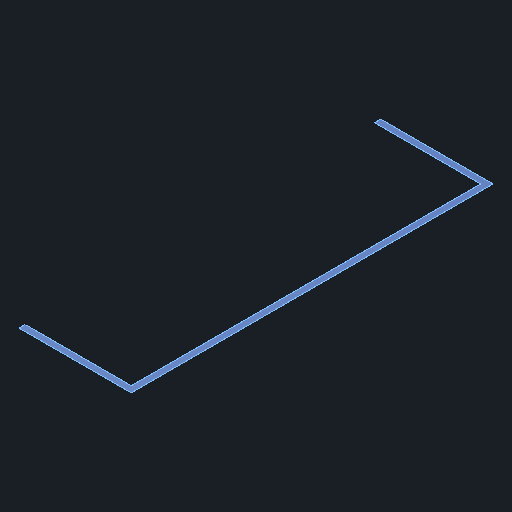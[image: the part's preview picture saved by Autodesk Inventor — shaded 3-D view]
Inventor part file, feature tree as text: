
AUTODESK INVENTOR PART (.ipt)
format: ipt  version: 2025 (Build 290162000, 162)  size: 80,384 bytes
history: native  units: in
note: dims shown in document units (in); Inventor stores cm internally (conversion verified against a paired STEP export)
features: extrude x1
ambient origin geometry x8: Origin, YZ Plane, XZ Plane, XY Plane, X Axis, Y Axis, Z Axis, Center Point
bodies: Solid1 (feature_tree)
feature tree (1):
  extrude  "Extrude-Thin1"  [1 undecoded]
note: 1 required parameter value undecoded (feature->parameter linkage not recoverable at this tier; creation-order binding heuristic only, values carry confidence <= 0.55)
